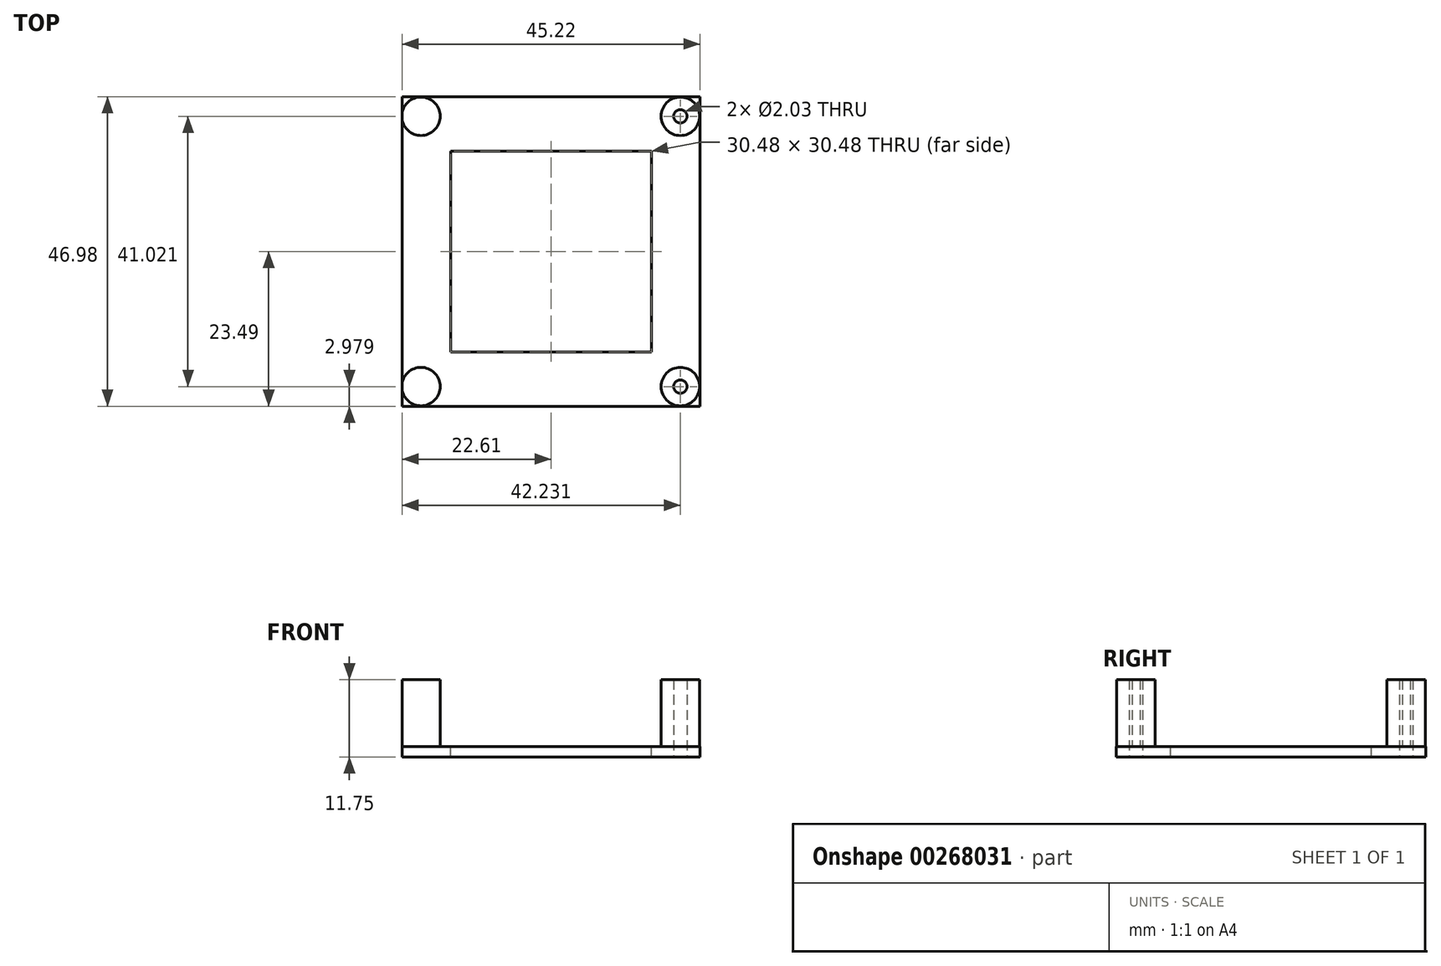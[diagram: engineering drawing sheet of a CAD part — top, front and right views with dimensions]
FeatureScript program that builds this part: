
annotation { "Feature Type Name" : "Feature", "Feature Type Description" : "" }
export const myFeature = defineFeature(function(context is Context, id is Id, definition is map)
    precondition{}
    {
        {
            var Q0;
            Q0=qCreatedBy(makeId("Top.planeOp"),FACE);
            var sketch = newSketch(context, id + "F0", { "sketchPlane" : qUnion([Q0])});
            skLineSegment(sketch, "E0.bottom", {"start": v(22.6, 23.5) * mm, "end": v(-22.6, 23.5) * mm});
            skLineSegment(sketch, "E0.top", {"start": v(22.6, -23.5) * mm, "end": v(-22.6, -23.5) * mm});
            skLineSegment(sketch, "E0.left", {"start": v(22.6, 23.5) * mm, "end": v(22.6, -23.5) * mm});
            skLineSegment(sketch, "E0.right", {"start": v(-22.6, 23.5) * mm, "end": v(-22.6, -23.5) * mm});
            skPoint(sketch, "E0.middle", {"position": v(0, 0) * mm});
            skSolve(sketch);
        }
        {
            var Q0;
            Q0=makeQuery(id+"F0.imprint","IMPRINT",FACE,{"disambiguationData":[TD([[makeQuery(id+"F0.imprint","IMPRINT",EDGE,{"derivedFrom":sQuery(id+"F0.wireOp",EDGE,"E0.bottom")}),1.0]])]});
            extrude(context, id + "F1", {"entities" : qUnion([Q0]), "depth" : 1.59 * mm});
        }
        {
            var Q0;
            Q0=makeQuery(id+"F1.opExtrude","CAP_FACE",FACE,{"disambiguationData":[OSD([sQuery(id+"F0.wireOp",EDGE,"E0.bottom"),sQuery(id+"F0.wireOp",EDGE,"E0.top"),sQuery(id+"F0.wireOp",EDGE,"E0.left"),sQuery(id+"F0.wireOp",EDGE,"E0.right")])],"isStart":false});
            var sketch = newSketch(context, id + "F2", { "sketchPlane" : qUnion([Q0])});
            skLineSegment(sketch, "E1.bottom", {"start": v(15.24, -15.24) * mm, "end": v(-15.24, -15.24) * mm});
            skLineSegment(sketch, "E1.top", {"start": v(15.24, 15.24) * mm, "end": v(-15.24, 15.24) * mm});
            skLineSegment(sketch, "E1.left", {"start": v(15.24, -15.24) * mm, "end": v(15.24, 15.24) * mm});
            skLineSegment(sketch, "E1.right", {"start": v(-15.24, -15.24) * mm, "end": v(-15.24, 15.24) * mm});
            skPoint(sketch, "E1.middle", {"position": v(0, 0) * mm});
            skSolve(sketch);
        }
        {
            var Q0;
            Q0=makeQuery(id+"F2.imprint","IMPRINT",FACE,{"disambiguationData":[TD([[makeQuery(id+"F2.imprint","IMPRINT",EDGE,{"derivedFrom":sQuery(id+"F2.wireOp",EDGE,"E1.bottom")}),-1.0]])]});
            extrude(context, id + "F3", {"entities" : qUnion([Q0]), "operationType" : NewBodyOperationType.REMOVE, "oppositeDirection" : true, "depth" : 6.35 * mm});
        }
        {
            var Q0;
            Q0=makeQuery(id+"F1.opExtrude","CAP_FACE",FACE,{"disambiguationData":[OSD([sQuery(id+"F0.wireOp",EDGE,"E0.bottom"),sQuery(id+"F0.wireOp",EDGE,"E0.top"),sQuery(id+"F0.wireOp",EDGE,"E0.left"),sQuery(id+"F0.wireOp",EDGE,"E0.right")])],"isStart":false});
            var sketch = newSketch(context, id + "F4", { "sketchPlane" : qUnion([Q0])});
            skLineSegment(sketch, "E2.bottom", {"start": v(19.62, -20.51) * mm, "end": v(22.6, -20.51) * mm, "construction": true});
            skLineSegment(sketch, "E2.top", {"start": v(19.62, -23.5) * mm, "end": v(22.6, -23.5) * mm, "construction": true});
            skLineSegment(sketch, "E2.left", {"start": v(19.62, -20.51) * mm, "end": v(19.62, -23.5) * mm, "construction": true});
            skLineSegment(sketch, "E2.right", {"start": v(22.6, -20.51) * mm, "end": v(22.6, -23.5) * mm, "construction": true});
            skCircle(sketch, "E3", {"center": v(19.62, -20.51) * mm, "radius": 1.02 * mm});
            skCircle(sketch, "E4", {"center": v(19.62, -20.51) * mm, "radius": 2.92 * mm});
            skLineSegment(sketch, "E5.bottom", {"start": v(19.62, -20.51) * mm, "end": v(-19.75, -20.51) * mm, "construction": true});
            skLineSegment(sketch, "E5.top", {"start": v(19.62, 20.51) * mm, "end": v(-19.75, 20.51) * mm, "construction": true});
            skLineSegment(sketch, "E5.left", {"start": v(19.62, -20.51) * mm, "end": v(19.62, 20.51) * mm, "construction": true});
            skLineSegment(sketch, "E5.right", {"start": v(-19.75, -20.51) * mm, "end": v(-19.75, 20.51) * mm, "construction": true});
            skCircle(sketch, "E6", {"center": v(-19.75, 20.51) * mm, "radius": 2.92 * mm});
            skCircle(sketch, "E7", {"center": v(19.62, 20.51) * mm, "radius": 1.02 * mm});
            skCircle(sketch, "E8", {"center": v(19.62, 20.51) * mm, "radius": 2.92 * mm});
            skCircle(sketch, "E9", {"center": v(-19.75, -20.51) * mm, "radius": 2.92 * mm});
            skLineSegment(sketch, "E10.bottom", {"start": v(22.6, -23.5) * mm, "end": v(-22.6, -23.5) * mm, "construction": true});
            skLineSegment(sketch, "E10.top", {"start": v(22.6, 23.5) * mm, "end": v(-22.6, 23.5) * mm, "construction": true});
            skLineSegment(sketch, "E10.left", {"start": v(22.6, -23.5) * mm, "end": v(22.6, 23.5) * mm, "construction": true});
            skLineSegment(sketch, "E10.right", {"start": v(-22.6, -23.5) * mm, "end": v(-22.6, 23.5) * mm, "construction": true});
            skSolve(sketch);
        }
        {
            var Q0;
            Q0=makeQuery(id+"F4.imprint","IMPRINT",FACE,{"disambiguationData":[TD([[makeQuery(id+"F4.imprint","IMPRINT",EDGE,{"derivedFrom":sQuery(id+"F4.wireOp",EDGE,"E7")}),-1.0]])]});
            var Q1;
            Q1=makeQuery(id+"F4.imprint","IMPRINT",FACE,{"disambiguationData":[TD([[makeQuery(id+"F4.imprint","IMPRINT",EDGE,{"derivedFrom":sQuery(id+"F4.wireOp",EDGE,"E3")}),-1.0]])]});
            var Q2;
            {var subQ0=sQuery(id+"F4.wireOp",EDGE,"E6");var subQ1=makeQuery(id+"F1.opExtrude","CAP_EDGE",EDGE,{"disambiguationData":[OSD([sQuery(id+"F0.wireOp",EDGE,"E0.right")])],"isStart":false});var subQ2=makeQuery(id+"F4.imprint","INTERSECT",VERTEX,{"disambiguationData":[OD(0.0)],"derivedFrom":[subQ1,subQ0]});Q2=makeQuery(id+"F4.imprint","IMPRINT",FACE,{"disambiguationData":[TD([[makeQuery(id+"F4.imprint","IMPRINT",EDGE,{"disambiguationData":[TD([[subQ2,1.0]])],"derivedFrom":subQ0}),1.0]])]});}
            var Q3;
            {var subQ0=sQuery(id+"F4.wireOp",EDGE,"E9");var subQ1=makeQuery(id+"F1.opExtrude","CAP_EDGE",EDGE,{"disambiguationData":[OSD([sQuery(id+"F0.wireOp",EDGE,"E0.right")])],"isStart":false});var subQ2=makeQuery(id+"F4.imprint","INTERSECT",VERTEX,{"disambiguationData":[OD(0.0)],"derivedFrom":[subQ1,subQ0]});Q3=makeQuery(id+"F4.imprint","IMPRINT",FACE,{"disambiguationData":[TD([[makeQuery(id+"F4.imprint","IMPRINT",EDGE,{"disambiguationData":[TD([[subQ2,-1.0]])],"derivedFrom":subQ0}),1.0]])]});}
            extrude(context, id + "F5", {"entities" : qUnion([Q0, Q1, Q2, Q3]), "operationType" : NewBodyOperationType.ADD, "depth" : 10.16 * mm});
        }
        {
            var Q0;
            Q0=makeQuery(id+"F4.imprint","IMPRINT",FACE,{"disambiguationData":[TD([[makeQuery(id+"F4.imprint","IMPRINT",EDGE,{"derivedFrom":sQuery(id+"F4.wireOp",EDGE,"E3")}),1.0]])]});
            var Q1;
            Q1=makeQuery(id+"F4.imprint","IMPRINT",FACE,{"disambiguationData":[TD([[makeQuery(id+"F4.imprint","IMPRINT",EDGE,{"derivedFrom":sQuery(id+"F4.wireOp",EDGE,"E7")}),1.0]])]});
            extrude(context, id + "F6", {"entities" : qUnion([Q0, Q1]), "operationType" : NewBodyOperationType.REMOVE, "oppositeDirection" : true, "depth" : 6.35 * mm});
        }
    });
